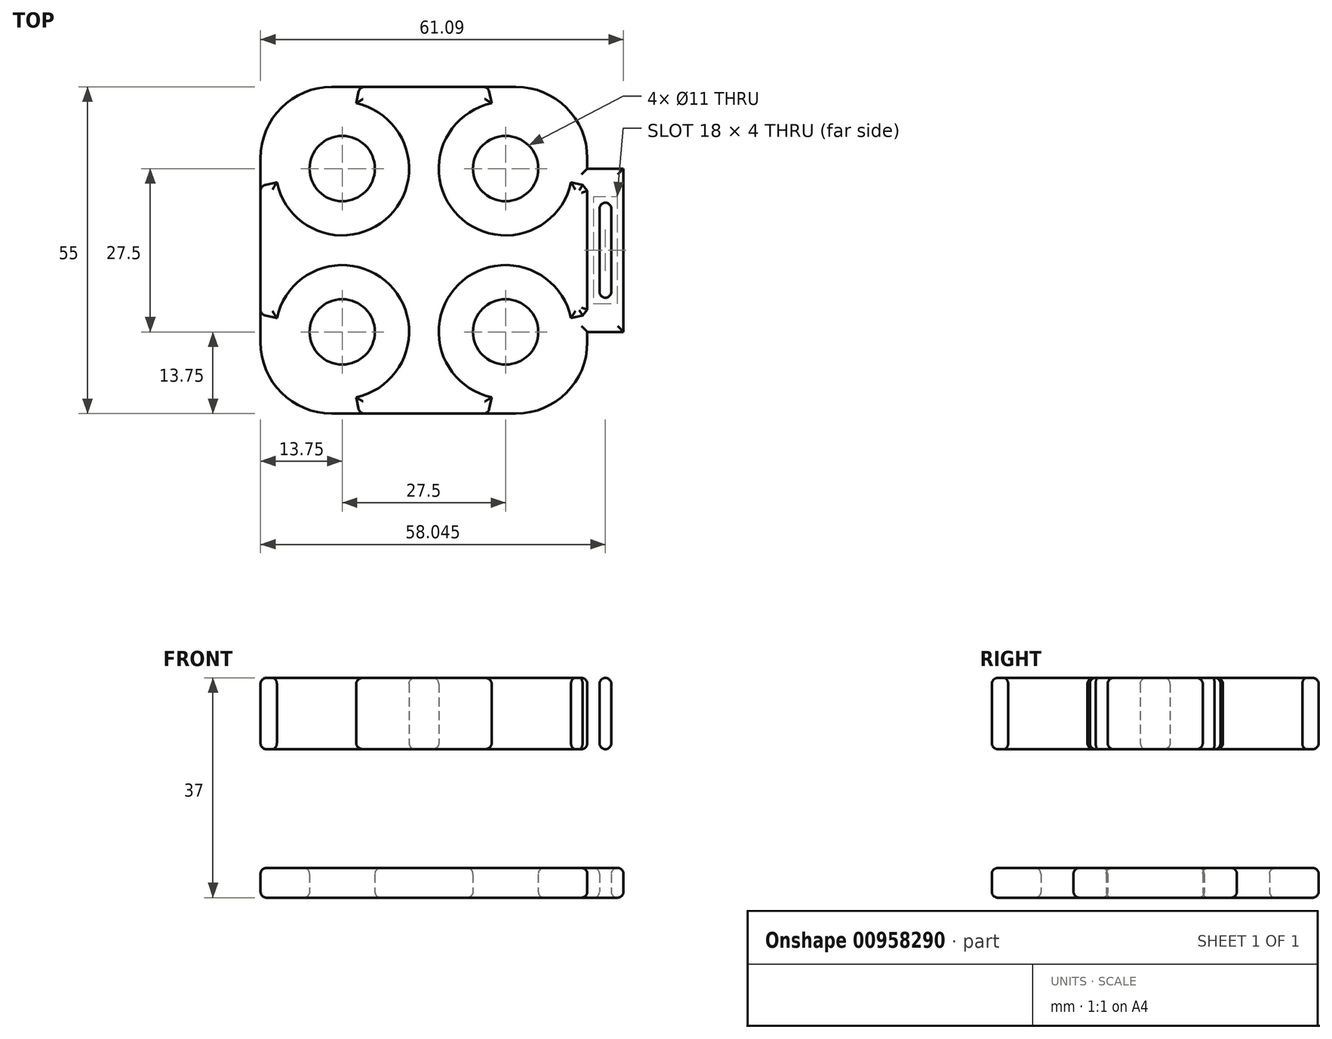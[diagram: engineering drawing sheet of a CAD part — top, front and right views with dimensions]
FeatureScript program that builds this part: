
annotation { "Feature Type Name" : "Feature", "Feature Type Description" : "" }
export const myFeature = defineFeature(function(context is Context, id is Id, definition is map)
    precondition{}
    {
        {
            var Q0;
            Q0=qCreatedBy(makeId("Top.planeOp"),FACE);
            var sketch = newSketch(context, id + "F0", { "sketchPlane" : qUnion([Q0])});
            skLineSegment(sketch, "E0.bottom", {"start": v(15.5, -27.5) * mm, "end": v(-15.5, -27.5) * mm});
            skLineSegment(sketch, "E0.top", {"start": v(15.5, 27.5) * mm, "end": v(-15.5, 27.5) * mm});
            skLineSegment(sketch, "E0.left", {"start": v(27.5, -15.5) * mm, "end": v(27.5, 15.5) * mm});
            skLineSegment(sketch, "E0.right", {"start": v(-27.5, -15.5) * mm, "end": v(-27.5, 15.5) * mm});
            skPoint(sketch, "E0.middle", {"position": v(0, 0) * mm});
            skLineSegment(sketch, "E1", {"start": v(-27.5, 0) * mm, "end": v(0, 0) * mm, "construction": true});
            skLineSegment(sketch, "E2", {"start": v(-13.75, 0) * mm, "end": v(-13.75, 27.5) * mm, "construction": true});
            skCircle(sketch, "E3", {"center": v(-13.75, 13.75) * mm, "radius": 5.5 * mm});
            skPoint(sketch, "E4.visualSharp", {"position": v(-27.5, 27.5) * mm});
            skArc(sketch, "E4.filletArc", {"start": v(-15.5, 27.5) * mm, "mid": v(-23.99, 23.99) * mm, "end": v(-27.5, 15.5) * mm});
            skPoint(sketch, "E5.visualSharp", {"position": v(27.5, 27.5) * mm});
            skArc(sketch, "E5.filletArc", {"start": v(27.5, 15.5) * mm, "mid": v(23.99, 23.99) * mm, "end": v(15.5, 27.5) * mm});
            skPoint(sketch, "E6.visualSharp", {"position": v(27.5, -27.5) * mm});
            skArc(sketch, "E6.filletArc", {"start": v(15.5, -27.5) * mm, "mid": v(23.99, -23.99) * mm, "end": v(27.5, -15.5) * mm});
            skPoint(sketch, "E7.visualSharp", {"position": v(-27.5, -27.5) * mm});
            skArc(sketch, "E7.filletArc", {"start": v(-27.5, -15.5) * mm, "mid": v(-23.99, -23.99) * mm, "end": v(-15.5, -27.5) * mm});
            skCircle(sketch, "E8.MirrorC", {"center": v(13.75, 13.75) * mm, "radius": 5.5 * mm});
            skCircle(sketch, "E9.MirrorC", {"center": v(-13.75, -13.75) * mm, "radius": 5.5 * mm});
            skCircle(sketch, "E10.MirrorC", {"center": v(13.75, -13.75) * mm, "radius": 5.5 * mm});
            skSolve(sketch);
        }
        {
            var Q0;
            Q0=qCreatedBy(makeId("Top.planeOp"),FACE);
            cPlane(context, id + "F1", {"entities" : qUnion([Q0]), "cplaneType" : CPlaneType.OFFSET, "offset" : 25 * mm, "width" : 150 * mm, "height" : 150 * mm});
        }
        {
            var Q0;
            Q0=qCreatedBy(id+"F1.planeOp",FACE);
            var sketch = newSketch(context, id + "F2", { "sketchPlane" : qUnion([Q0])});
            skLineSegment(sketch, "E11.0.1", {"start": v(13.75, 27.5) * mm, "end": v(-10.83, 27.5) * mm});
            skLineSegment(sketch, "E11.0.3", {"start": v(-27.5, 10.83) * mm, "end": v(-27.5, -13.75) * mm});
            skLineSegment(sketch, "E11.0.5", {"start": v(-13.75, -27.5) * mm, "end": v(13.75, -27.5) * mm});
            skLineSegment(sketch, "E11.0.7", {"start": v(27.5, -13.75) * mm, "end": v(27.5, 13.75) * mm});
            skLineSegment(sketch, "E12.0", {"start": v(-13.75, 0) * mm, "end": v(-13.75, 25) * mm, "construction": true});
            skLineSegment(sketch, "E13.0", {"start": v(-27.5, 0) * mm, "end": v(0, 0) * mm, "construction": true});
            skArc(sketch, "E14", {"start": v(-24.75, 11.41) * mm, "mid": v(-5.8, 5.8) * mm, "end": v(-11.41, 24.75) * mm});
            skPoint(sketch, "E15", {"position": v(-13.75, 25) * mm});
            skPoint(sketch, "E16", {"position": v(-13.75, 2.5) * mm});
            skLineSegment(sketch, "E17", {"start": v(-13.75, 13.75) * mm, "end": v(-25, 13.75) * mm, "construction": true});
            skPoint(sketch, "E18.orphan", {"position": v(-27.5, 15.5) * mm});
            skPoint(sketch, "E19.orphan", {"position": v(-15.5, 27.5) * mm});
            skArc(sketch, "E20.MirrorCS", {"start": v(25, 13.75) * mm, "mid": v(5.8, 5.8) * mm, "end": v(13.75, 25) * mm});
            skArc(sketch, "E21.MirrorCS", {"start": v(-25, -13.75) * mm, "mid": v(-5.8, -5.8) * mm, "end": v(-13.75, -25) * mm});
            skArc(sketch, "E22.MirrorCS", {"start": v(25, -13.75) * mm, "mid": v(5.8, -5.8) * mm, "end": v(13.75, -25) * mm});
            skPoint(sketch, "E23.orphan", {"position": v(-27.5, -15.5) * mm});
            skPoint(sketch, "E24.orphan", {"position": v(-15.5, -27.5) * mm});
            skPoint(sketch, "E25.orphan", {"position": v(15.5, -27.5) * mm});
            skPoint(sketch, "E26.orphan", {"position": v(27.5, -15.5) * mm});
            skPoint(sketch, "E27.orphan", {"position": v(27.5, 15.5) * mm});
            skPoint(sketch, "E28.orphan", {"position": v(15.5, 27.5) * mm});
            skPoint(sketch, "E29", {"position": v(-24.75, 11.41) * mm});
            skPoint(sketch, "E30", {"position": v(-11.41, 24.75) * mm});
            skLineSegment(sketch, "E31", {"start": v(-13.75, 13.75) * mm, "end": v(-11.41, 24.75) * mm, "construction": true});
            skLineSegment(sketch, "E32", {"start": v(-13.75, 13.75) * mm, "end": v(-24.75, 11.41) * mm, "construction": true});
            skLineSegment(sketch, "E33", {"start": v(-11.41, 24.75) * mm, "end": v(-10.83, 27.5) * mm});
            skLineSegment(sketch, "E34", {"start": v(-24.75, 11.41) * mm, "end": v(-27.5, 10.83) * mm});
            skPoint(sketch, "E35.orphan", {"position": v(-13.75, 27.5) * mm});
            skPoint(sketch, "E36.end.orphan", {"position": v(-27.5, 13.75) * mm});
            skLineSegment(sketch, "E37.MirrorCS", {"start": v(11.41, 24.75) * mm, "end": v(10.83, 27.5) * mm});
            skLineSegment(sketch, "E38.MirrorCS", {"start": v(24.75, 11.41) * mm, "end": v(27.5, 10.83) * mm});
            skLineSegment(sketch, "E39.MirrorCS", {"start": v(-24.75, -11.41) * mm, "end": v(-27.5, -10.83) * mm});
            skLineSegment(sketch, "E40.MirrorCS", {"start": v(-11.41, -24.75) * mm, "end": v(-10.83, -27.5) * mm});
            skLineSegment(sketch, "E41.MirrorCS", {"start": v(24.75, -11.41) * mm, "end": v(27.5, -10.83) * mm});
            skLineSegment(sketch, "E42.MirrorCS", {"start": v(11.41, -24.75) * mm, "end": v(10.83, -27.5) * mm});
            skPoint(sketch, "E43.MirrorCS.start.orphan", {"position": v(-13.75, -25) * mm});
            skPoint(sketch, "E44.MirrorCS.start.orphan", {"position": v(-25, -13.75) * mm});
            skPoint(sketch, "E45.MirrorCS.start.orphan", {"position": v(13.75, -25) * mm});
            skPoint(sketch, "E46.MirrorCS.start.orphan", {"position": v(25, -13.75) * mm});
            skPoint(sketch, "E47.MirrorCS.start.orphan", {"position": v(25, 13.75) * mm});
            skPoint(sketch, "E48.MirrorCS.start.orphan", {"position": v(13.75, 25) * mm});
            skSolve(sketch);
        }
        {
            var Q0;
            Q0=makeQuery(id+"F0.imprint","IMPRINT",FACE,{"disambiguationData":[TD([[makeQuery(id+"F0.imprint","IMPRINT",EDGE,{"derivedFrom":sQuery(id+"F0.wireOp",EDGE,"E0.bottom")}),-1.0]])]});
            extrude(context, id + "F3", {"entities" : qUnion([Q0]), "depth" : 5 * mm, "offsetDistance" : 25 * mm});
        }
        {
            var Q0;
            Q0=makeQuery(id+"F2.imprint","IMPRINT",FACE,{"disambiguationData":[TD([[makeQuery(id+"F2.imprint","IMPRINT",EDGE,{"derivedFrom":sQuery(id+"F2.wireOp",EDGE,"E11.0.1")}),1.0]])]});
            extrude(context, id + "F4", {"entities" : qUnion([Q0]), "depth" : 12 * mm, "offsetDistance" : 25 * mm});
        }
        {
            var Q0;
            Q0=makeQuery(id+"F4.opExtrude","SWEPT_FACE",FACE,{"disambiguationData":[OSD([sQuery(id+"F2.wireOp",EDGE,"E11.0.5")])]});
            var sketch = newSketch(context, id + "F5", { "sketchPlane" : qUnion([Q0])});
            skLineSegment(sketch, "E49", {"start": v(0, 25) * mm, "end": v(0, 37) * mm, "construction": true});
            skPoint(sketch, "E50", {"position": v(0, 31) * mm});
            skSolve(sketch);
        }
        {
            var Q0;
            Q0=sQuery(id+"F5.wireOp",VERTEX,"E50");
            var Q1;
            Q1=qCreatedBy(makeId("Top.planeOp"),FACE);
            cPlane(context, id + "F6", {"entities" : qUnion([Q0, Q1]), "cplaneType" : CPlaneType.PLANE_POINT, "offset" : 25 * mm, "width" : 150 * mm, "height" : 150 * mm});
        }
        {
            var Q0;
            Q0=makeQuery(id+"F4.opExtrude","CAP_FACE",FACE,{"disambiguationData":[OSD([sQuery(id+"F2.wireOp",EDGE,"E11.0.1"),sQuery(id+"F2.wireOp",EDGE,"E11.0.3"),sQuery(id+"F2.wireOp",EDGE,"E11.0.5"),sQuery(id+"F2.wireOp",EDGE,"E11.0.7"),sQuery(id+"F2.wireOp",EDGE,"E14"),sQuery(id+"F2.wireOp",EDGE,"E36"),sQuery(id+"F2.wireOp",EDGE,"qw1fORpv-z2hO-5Xj9-ntVv-7LOXdHvMgr3n"),sQuery(id+"F2.wireOp",EDGE,"E20.MirrorCS"),sQuery(id+"F2.wireOp",EDGE,"E48.MirrorCS"),sQuery(id+"F2.wireOp",EDGE,"E47.MirrorCS"),sQuery(id+"F2.wireOp",EDGE,"E21.MirrorCS"),sQuery(id+"F2.wireOp",EDGE,"E22.MirrorCS"),sQuery(id+"F2.wireOp",EDGE,"E43.MirrorCS"),sQuery(id+"F2.wireOp",EDGE,"E44.MirrorCS"),sQuery(id+"F2.wireOp",EDGE,"E45.MirrorCS"),sQuery(id+"F2.wireOp",EDGE,"E46.MirrorCS")])],"isStart":false});
            var sketch = newSketch(context, id + "F7", { "sketchPlane" : qUnion([Q0])});
            skLineSegment(sketch, "E51", {"start": v(27.5, 10.83) * mm, "end": v(27.5, 10.83) * mm});
            skPoint(sketch, "E52", {"position": v(30.54, -10) * mm});
            skPoint(sketch, "E53", {"position": v(30.54, 10.83) * mm});
            skLineSegment(sketch, "E54", {"start": v(30.54, -10) * mm, "end": v(30.54, -7) * mm, "construction": true});
            skLineSegment(sketch, "E55", {"start": v(30.54, 10.83) * mm, "end": v(30.54, 7) * mm, "construction": true});
            skLineSegment(sketch, "E56", {"start": v(30.54, -7) * mm, "end": v(30.54, 7) * mm});
            skArc(sketch, "E57.0.startCap", {"start": v(31.54, -7) * mm, "mid": v(30.54, -8) * mm, "end": v(29.54, -7) * mm});
            skArc(sketch, "E57.0.endCap", {"start": v(29.54, 7) * mm, "mid": v(30.54, 8) * mm, "end": v(31.54, 7) * mm});
            skLineSegment(sketch, "E57.0.left", {"start": v(29.54, -7) * mm, "end": v(29.54, 7) * mm});
            skLineSegment(sketch, "E57.0.right", {"start": v(31.54, -7) * mm, "end": v(31.54, 7) * mm});
            skPoint(sketch, "E58", {"position": v(30.54, 0) * mm});
            skLineSegment(sketch, "E59", {"start": v(27.5, 10.24) * mm, "end": v(34.16, 10.24) * mm});
            skLineSegment(sketch, "E60", {"start": v(34.16, 10.24) * mm, "end": v(34.16, -10.24) * mm});
            skLineSegment(sketch, "E61", {"start": v(34.16, -10.24) * mm, "end": v(27.5, -10.24) * mm});
            skLineSegment(sketch, "E62", {"start": v(27.5, -10.24) * mm, "end": v(27.5, 10.24) * mm});
            skSolve(sketch);
        }
        {
            var Q0;
            Q0=makeQuery(id+"F7.imprint","IMPRINT",FACE,{"disambiguationData":[TD([[makeQuery(id+"F7.imprint","IMPRINT",EDGE,{"derivedFrom":sQuery(id+"F7.wireOp",EDGE,"E51")}),-1.0]])]});
            var Q1;
            Q1=makeQuery(id+"F7.imprint","IMPRINT",FACE,{"disambiguationData":[TD([[makeQuery(id+"F7.imprint","IMPRINT",EDGE,{"derivedFrom":sQuery(id+"F7.wireOp",EDGE,"E57.0.startCap")}),1.0]])]});
            var Q2;
            {var subQ0=sQuery(id+"F2.wireOp",EDGE,"E46.MirrorCS");var subQ1=sQuery(id+"F2.wireOp",EDGE,"E22.MirrorCS");var subQ2=sQuery(id+"F2.wireOp",EDGE,"E48.MirrorCS");var subQ3=sQuery(id+"F2.wireOp",EDGE,"E47.MirrorCS");var subQ4=sQuery(id+"F2.wireOp",EDGE,"E11.0.1");var subQ5=sQuery(id+"F2.wireOp",EDGE,"E45.MirrorCS");var subQ6=sQuery(id+"F2.wireOp",EDGE,"E11.0.7");var subQ7=sQuery(id+"F2.wireOp",EDGE,"E11.0.5");var subQ8=sQuery(id+"F2.wireOp",EDGE,"E20.MirrorCS");Q2=makeQuery(id+"FFjtNiAkE0yxe9r_2.boolean.opBoolean","SPLIT",FACE,{"disambiguationData":[TD([makeQuery(id+"F4.opExtrude","SWEPT_FACE",FACE,{"disambiguationData":[OSD([subQ6])]})])],"derivedFrom":makeQuery(id+"F4.opExtrude","CAP_FACE",FACE,{"disambiguationData":[OSD([subQ4,sQuery(id+"F2.wireOp",EDGE,"E11.0.3"),subQ7,subQ6,sQuery(id+"F2.wireOp",EDGE,"E14"),sQuery(id+"F2.wireOp",EDGE,"E36"),sQuery(id+"F2.wireOp",EDGE,"qw1fORpv-z2hO-5Xj9-ntVv-7LOXdHvMgr3n"),subQ8,subQ2,subQ3,sQuery(id+"F2.wireOp",EDGE,"E21.MirrorCS"),subQ1,sQuery(id+"F2.wireOp",EDGE,"E43.MirrorCS"),sQuery(id+"F2.wireOp",EDGE,"E44.MirrorCS"),subQ5,subQ0])],"isStart":true})});}
            extrude(context, id + "F8", {"entities" : qUnion([Q0, Q1]), "operationType" : NewBodyOperationType.ADD, "endBound" : BoundingType.UP_TO_SURFACE, "oppositeDirection" : true, "depth" : 25 * mm, "endBoundEntityFace" : qUnion([Q2]), "offsetDistance" : 25 * mm});
        }
        {
            var Q0;
            Q0=makeQuery(id+"F3.opExtrude","CAP_FACE",FACE,{"disambiguationData":[OSD([sQuery(id+"F0.wireOp",EDGE,"E0.bottom"),sQuery(id+"F0.wireOp",EDGE,"E0.top"),sQuery(id+"F0.wireOp",EDGE,"E0.left"),sQuery(id+"F0.wireOp",EDGE,"E0.right"),sQuery(id+"F0.wireOp",EDGE,"E3"),sQuery(id+"F0.wireOp",EDGE,"E4.filletArc"),sQuery(id+"F0.wireOp",EDGE,"E5.filletArc"),sQuery(id+"F0.wireOp",EDGE,"E6.filletArc"),sQuery(id+"F0.wireOp",EDGE,"E7.filletArc"),sQuery(id+"F0.wireOp",EDGE,"E8.MirrorC"),sQuery(id+"F0.wireOp",EDGE,"E9.MirrorC"),sQuery(id+"F0.wireOp",EDGE,"E10.MirrorC")])],"isStart":true});
            var sketch = newSketch(context, id + "F9", { "sketchPlane" : qUnion([Q0])});
            skLineSegment(sketch, "E63.0", {"start": v(29.54, -7) * mm, "end": v(29.54, 7) * mm});
            skArc(sketch, "E64.0", {"start": v(29.54, 7) * mm, "mid": v(30.54, 8) * mm, "end": v(31.54, 7) * mm});
            skLineSegment(sketch, "E65.0", {"start": v(31.54, -7) * mm, "end": v(31.54, 7) * mm});
            skArc(sketch, "E66.0", {"start": v(31.54, -7) * mm, "mid": v(30.54, -8) * mm, "end": v(29.54, -7) * mm});
            skLineSegment(sketch, "E67.0", {"start": v(27.5, 15.5) * mm, "end": v(27.5, -15.5) * mm});
            skLineSegment(sketch, "E68.0", {"start": v(33.59, 13.75) * mm, "end": v(27.5, 13.75) * mm});
            skLineSegment(sketch, "E69.0", {"start": v(27.5, -13.75) * mm, "end": v(33.59, -13.75) * mm});
            skLineSegment(sketch, "E70", {"start": v(33.59, 13.75) * mm, "end": v(33.59, -13.75) * mm});
            skSolve(sketch);
        }
        {
            var Q0;
            Q0=makeQuery(id+"F9.imprint","IMPRINT",FACE,{"disambiguationData":[TD([[makeQuery(id+"F9.imprint","IMPRINT",EDGE,{"derivedFrom":sQuery(id+"F9.wireOp",EDGE,"E63.0")}),1.0]])]});
            var Q1;
            Q1=makeQuery(id+"F3.opExtrude","CAP_FACE",FACE,{"disambiguationData":[OSD([sQuery(id+"F0.wireOp",EDGE,"E0.bottom"),sQuery(id+"F0.wireOp",EDGE,"E0.top"),sQuery(id+"F0.wireOp",EDGE,"E0.left"),sQuery(id+"F0.wireOp",EDGE,"E0.right"),sQuery(id+"F0.wireOp",EDGE,"E3"),sQuery(id+"F0.wireOp",EDGE,"E4.filletArc"),sQuery(id+"F0.wireOp",EDGE,"E5.filletArc"),sQuery(id+"F0.wireOp",EDGE,"E6.filletArc"),sQuery(id+"F0.wireOp",EDGE,"E7.filletArc"),sQuery(id+"F0.wireOp",EDGE,"E8.MirrorC"),sQuery(id+"F0.wireOp",EDGE,"E9.MirrorC"),sQuery(id+"F0.wireOp",EDGE,"E10.MirrorC")])],"isStart":false});
            extrude(context, id + "F10", {"entities" : qUnion([Q0]), "operationType" : NewBodyOperationType.ADD, "endBound" : BoundingType.UP_TO_SURFACE, "oppositeDirection" : true, "depth" : 25 * mm, "endBoundEntityFace" : qUnion([Q1]), "offsetDistance" : 25 * mm});
        }
        {
            var Q0;
            Q0=makeQuery(id+"F3.opExtrude","CAP_EDGE",EDGE,{"disambiguationData":[OSD([sQuery(id+"F0.wireOp",EDGE,"E0.right")])],"isStart":true});
            var Q1;
            Q1=makeQuery(id+"F3.opExtrude","CAP_FACE",FACE,{"disambiguationData":[OSD([sQuery(id+"F0.wireOp",EDGE,"E0.bottom"),sQuery(id+"F0.wireOp",EDGE,"E0.top"),sQuery(id+"F0.wireOp",EDGE,"E0.left"),sQuery(id+"F0.wireOp",EDGE,"E0.right"),sQuery(id+"F0.wireOp",EDGE,"E3"),sQuery(id+"F0.wireOp",EDGE,"E4.filletArc"),sQuery(id+"F0.wireOp",EDGE,"E5.filletArc"),sQuery(id+"F0.wireOp",EDGE,"E6.filletArc"),sQuery(id+"F0.wireOp",EDGE,"E7.filletArc"),sQuery(id+"F0.wireOp",EDGE,"E8.MirrorC"),sQuery(id+"F0.wireOp",EDGE,"E9.MirrorC"),sQuery(id+"F0.wireOp",EDGE,"E10.MirrorC")])],"isStart":true});
            var Q2;
            Q2=makeQuery(id+"F3.opExtrude","CAP_EDGE",EDGE,{"disambiguationData":[OSD([sQuery(id+"F0.wireOp",EDGE,"E0.bottom")])],"isStart":false});
            var Q3;
            Q3=makeQuery(id+"F3.opExtrude","CAP_EDGE",EDGE,{"disambiguationData":[OSD([sQuery(id+"F0.wireOp",EDGE,"E7.filletArc")])],"isStart":false});
            var Q4;
            Q4=makeQuery(id+"F10.opExtrude","CAP_EDGE",EDGE,{"disambiguationData":[OSD([sQuery(id+"F9.wireOp",EDGE,"E63.0")])],"isStart":false});
            fillet(context, id + "F11", {"entities" : qUnion([Q0, Q1, Q2, Q3, Q4]), "radius" : 1 * mm, "tangentPropagation" : true, "allowEdgeOverflow" : false});
        }
        {
            var Q0;
            Q0=makeQuery(id+"F8.opExtrude","CAP_EDGE",EDGE,{"disambiguationData":[OSD([sQuery(id+"F7.wireOp",EDGE,"E57.0.right")])],"isStart":true});
            var Q1;
            Q1=makeQuery(id+"F8.opExtrude","CAP_EDGE",EDGE,{"disambiguationData":[OSD([sQuery(id+"F7.wireOp",EDGE,"E57.0.right")])],"isStart":false});
            var Q2;
            Q2=makeQuery(id+"F8.opExtrude","CAP_EDGE",EDGE,{"disambiguationData":[OSD([sQuery(id+"F7.wireOp",EDGE,"E51")])],"isStart":false});
            var Q3;
            Q3=makeQuery(id+"F4.opExtrude","CAP_EDGE",EDGE,{"disambiguationData":[OSD([sQuery(id+"F2.wireOp",EDGE,"E11.0.5")])],"isStart":true});
            var Q4;
            Q4=makeQuery(id+"F4.opExtrude","CAP_EDGE",EDGE,{"disambiguationData":[OSD([sQuery(id+"F2.wireOp",EDGE,"E11.0.1")])],"isStart":true});
            var Q5;
            Q5=makeQuery(id+"F4.opExtrude","CAP_EDGE",EDGE,{"disambiguationData":[OSD([sQuery(id+"F2.wireOp",EDGE,"E11.0.3")])],"isStart":true});
            fillet(context, id + "F12", {"entities" : qUnion([Q0, Q1, Q2, Q3, Q4, Q5]), "radius" : 1 * mm, "tangentPropagation" : true, "allowEdgeOverflow" : false});
        }
        {
            var Q0;
            Q0=makeQuery(id+"F4.opExtrude","SWEPT_EDGE",EDGE,{"disambiguationData":[OSD([sQuery(id+"F2.wireOp",EDGE,"E11.0.7"),sQuery(id+"F2.wireOp",EDGE,"E38.MirrorCS")])]});
            var Q1;
            Q1=makeQuery(id+"F4.opExtrude","SWEPT_EDGE",EDGE,{"disambiguationData":[OSD([sQuery(id+"F2.wireOp",EDGE,"E11.0.7"),sQuery(id+"F2.wireOp",EDGE,"E41.MirrorCS")])]});
            chamfer(context, id + "F13", {"entities" : qUnion([Q0, Q1]), "width" : 1 * mm, "tangentPropagation" : true});
        }
        {
            var Q0;
            Q0=makeQuery(id+"F8.boolean.opBoolean","MERGE",FACE,{"derivedFrom":[makeQuery(id+"F4.opExtrude","CAP_FACE",FACE,{"disambiguationData":[OSD([sQuery(id+"F2.wireOp",EDGE,"E11.0.1"),sQuery(id+"F2.wireOp",EDGE,"E11.0.3"),sQuery(id+"F2.wireOp",EDGE,"E11.0.5"),sQuery(id+"F2.wireOp",EDGE,"E11.0.7"),sQuery(id+"F2.wireOp",EDGE,"E14"),sQuery(id+"F2.wireOp",EDGE,"E20.MirrorCS"),sQuery(id+"F2.wireOp",EDGE,"E21.MirrorCS"),sQuery(id+"F2.wireOp",EDGE,"E22.MirrorCS"),sQuery(id+"F2.wireOp",EDGE,"E33"),sQuery(id+"F2.wireOp",EDGE,"E34"),sQuery(id+"F2.wireOp",EDGE,"E37.MirrorCS"),sQuery(id+"F2.wireOp",EDGE,"E38.MirrorCS"),sQuery(id+"F2.wireOp",EDGE,"E39.MirrorCS"),sQuery(id+"F2.wireOp",EDGE,"E40.MirrorCS"),sQuery(id+"F2.wireOp",EDGE,"E41.MirrorCS"),sQuery(id+"F2.wireOp",EDGE,"E42.MirrorCS")])],"isStart":false}),makeQuery(id+"F8.opExtrude","CAP_FACE",FACE,{"disambiguationData":[OSD([sQuery(id+"F7.wireOp",EDGE,"E57.0.startCap"),sQuery(id+"F7.wireOp",EDGE,"E57.0.endCap"),sQuery(id+"F7.wireOp",EDGE,"E57.0.left"),sQuery(id+"F7.wireOp",EDGE,"E57.0.right"),sQuery(id+"F7.wireOp",EDGE,"E59"),sQuery(id+"F7.wireOp",EDGE,"E60"),sQuery(id+"F7.wireOp",EDGE,"E61"),sQuery(id+"F7.wireOp",EDGE,"E62")])],"isStart":true})]});
            var Q1;
            Q1=makeQuery(id+"F8.boolean.opBoolean","MERGE",FACE,{"derivedFrom":[makeQuery(id+"F4.opExtrude","CAP_FACE",FACE,{"disambiguationData":[OSD([sQuery(id+"F2.wireOp",EDGE,"E11.0.1"),sQuery(id+"F2.wireOp",EDGE,"E11.0.3"),sQuery(id+"F2.wireOp",EDGE,"E11.0.5"),sQuery(id+"F2.wireOp",EDGE,"E11.0.7"),sQuery(id+"F2.wireOp",EDGE,"E14"),sQuery(id+"F2.wireOp",EDGE,"E20.MirrorCS"),sQuery(id+"F2.wireOp",EDGE,"E21.MirrorCS"),sQuery(id+"F2.wireOp",EDGE,"E22.MirrorCS"),sQuery(id+"F2.wireOp",EDGE,"E33"),sQuery(id+"F2.wireOp",EDGE,"E34"),sQuery(id+"F2.wireOp",EDGE,"E37.MirrorCS"),sQuery(id+"F2.wireOp",EDGE,"E38.MirrorCS"),sQuery(id+"F2.wireOp",EDGE,"E39.MirrorCS"),sQuery(id+"F2.wireOp",EDGE,"E40.MirrorCS"),sQuery(id+"F2.wireOp",EDGE,"E41.MirrorCS"),sQuery(id+"F2.wireOp",EDGE,"E42.MirrorCS")])],"isStart":true}),makeQuery(id+"F8.opExtrude","CAP_FACE",FACE,{"disambiguationData":[OSD([sQuery(id+"F7.wireOp",EDGE,"E57.0.startCap"),sQuery(id+"F7.wireOp",EDGE,"E57.0.endCap"),sQuery(id+"F7.wireOp",EDGE,"E57.0.left"),sQuery(id+"F7.wireOp",EDGE,"E57.0.right"),sQuery(id+"F7.wireOp",EDGE,"E59"),sQuery(id+"F7.wireOp",EDGE,"E60"),sQuery(id+"F7.wireOp",EDGE,"E61"),sQuery(id+"F7.wireOp",EDGE,"E62")])],"isStart":false})]});
            fillet(context, id + "F14", {"entities" : qUnion([Q0, Q1]), "radius" : 1 * mm, "tangentPropagation" : true, "allowEdgeOverflow" : false});
        }
        {
            var Q0;
            Q0=makeQuery(id+"F10.boolean.opBoolean","MERGE",FACE,{"derivedFrom":[makeQuery(id+"F3.opExtrude","CAP_FACE",FACE,{"disambiguationData":[OSD([sQuery(id+"F0.wireOp",EDGE,"E0.bottom"),sQuery(id+"F0.wireOp",EDGE,"E0.top"),sQuery(id+"F0.wireOp",EDGE,"E0.left"),sQuery(id+"F0.wireOp",EDGE,"E0.right"),sQuery(id+"F0.wireOp",EDGE,"E3"),sQuery(id+"F0.wireOp",EDGE,"E4.filletArc"),sQuery(id+"F0.wireOp",EDGE,"E5.filletArc"),sQuery(id+"F0.wireOp",EDGE,"E6.filletArc"),sQuery(id+"F0.wireOp",EDGE,"E7.filletArc"),sQuery(id+"F0.wireOp",EDGE,"E8.MirrorC"),sQuery(id+"F0.wireOp",EDGE,"E9.MirrorC"),sQuery(id+"F0.wireOp",EDGE,"E10.MirrorC")])],"isStart":false}),makeQuery(id+"F10.opExtrude","CAP_FACE",FACE,{"disambiguationData":[OSD([sQuery(id+"F9.wireOp",EDGE,"E63.0"),sQuery(id+"F9.wireOp",EDGE,"E64.0"),sQuery(id+"F9.wireOp",EDGE,"E65.0"),sQuery(id+"F9.wireOp",EDGE,"E66.0"),sQuery(id+"F9.wireOp",EDGE,"E67.0"),sQuery(id+"F9.wireOp",EDGE,"E68.0"),sQuery(id+"F9.wireOp",EDGE,"E69.0"),sQuery(id+"F9.wireOp",EDGE,"E70")])],"isStart":false})]});
            fillet(context, id + "F15", {"entities" : qUnion([Q0]), "radius" : 1 * mm, "tangentPropagation" : true, "allowEdgeOverflow" : false});
        }
    });
